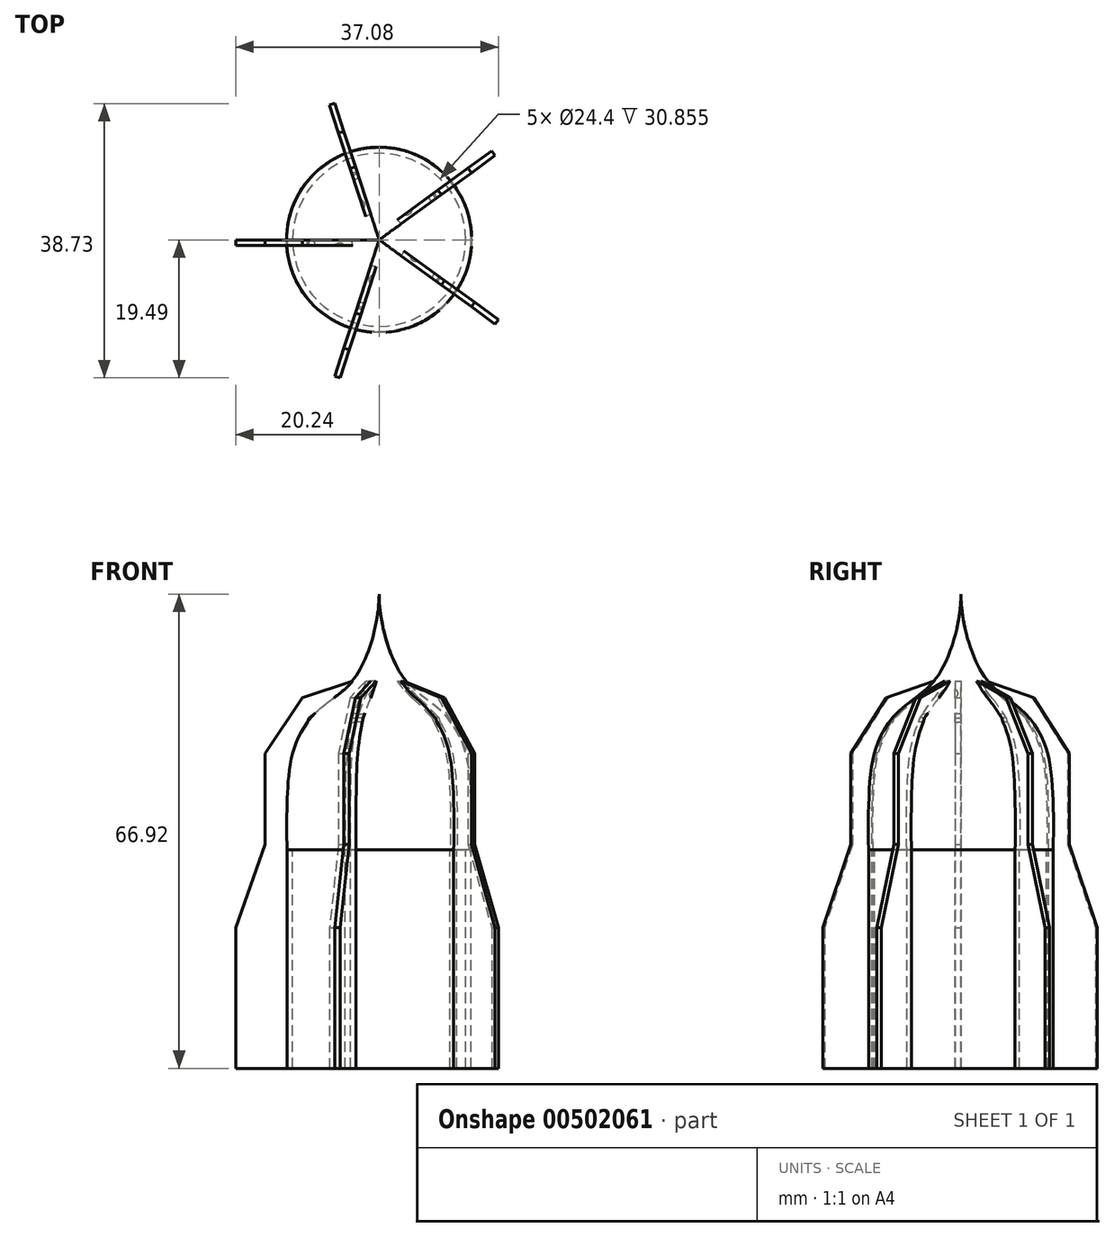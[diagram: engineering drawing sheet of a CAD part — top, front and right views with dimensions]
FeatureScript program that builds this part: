
annotation { "Feature Type Name" : "Feature", "Feature Type Description" : "" }
export const myFeature = defineFeature(function(context is Context, id is Id, definition is map)
    precondition{}
    {
        {
            var Q0;
            Q0=qCreatedBy(makeId("Front.planeOp"),FACE);
            var sketch = newSketch(context, id + "F0", { "sketchPlane" : qUnion([Q0])});
            skLineSegment(sketch, "E0", {"start": v(-12.2, 0) * mm, "end": v(-12.2, 30.85) * mm});
            skLineSegment(sketch, "E1", {"start": v(-13, 0) * mm, "end": v(-13, 30.85) * mm});
            skLineSegment(sketch, "E2", {"start": v(-12.2, 0) * mm, "end": v(-13, 0) * mm});
            skFitSpline(sketch, "E3", {"points": [v(-13, 30.85) * mm, v(-13, 37.68) * mm, v(-12.08, 45) * mm, v(-8.62, 50.53) * mm, v(-3.36, 55.23) * mm, v(0, 66.92) * mm], "startDerivative": vector(-1.92, 37.82) * mm, "endDerivative": vector(0, 44.37) * mm});
            skLineSegment(sketch, "E4", {"start": v(-12.2, 30.85) * mm, "end": v(0, 30.85) * mm});
            skLineSegment(sketch, "E5", {"start": v(0, 71.14) * mm, "end": v(0, -27.48) * mm});
            skSolve(sketch);
        }
        {
            var Q0;
            Q0=makeQuery(id+"F0.imprint","IMPRINT",FACE,{"disambiguationData":[TD([[makeQuery(id+"F0.imprint","IMPRINT",EDGE,{"derivedFrom":sQuery(id+"F0.wireOp",EDGE,"E0")}),1.0]])]});
            var Q1;
            Q1=sQuery(id+"F0.wireOp",EDGE,"E5");
            revolve(context, id + "F1", {"entities" : qUnion([Q0]), "axis" : qUnion([Q1]), "revolveType" : RevolveType.FULL});
        }
        {
            var Q0;
            Q0=qCreatedBy(makeId("Front.planeOp"),FACE);
            var sketch = newSketch(context, id + "F2", { "sketchPlane" : qUnion([Q0])});
            skLineSegment(sketch, "E6", {"start": v(-3.22, 54.82) * mm, "end": v(-10.83, 52.33) * mm});
            skLineSegment(sketch, "E7", {"start": v(-10.83, 52.33) * mm, "end": v(-16.09, 44.45) * mm});
            skLineSegment(sketch, "E8", {"start": v(-16.09, 44.45) * mm, "end": v(-16.09, 31.59) * mm});
            skLineSegment(sketch, "E9", {"start": v(-16.09, 31.59) * mm, "end": v(-20.24, 19.83) * mm});
            skLineSegment(sketch, "E10", {"start": v(-20.24, 19.83) * mm, "end": v(-20.24, 0) * mm});
            skLineSegment(sketch, "E11", {"start": v(-20.24, 0) * mm, "end": v(-12.63, 0) * mm});
            skLineSegment(sketch, "E12", {"start": v(-12.63, 0) * mm, "end": v(-12.63, 30.62) * mm});
            skLineSegment(sketch, "E13", {"start": v(-12.63, 30.62) * mm, "end": v(-12.63, 34.35) * mm});
            skLineSegment(sketch, "E14", {"start": v(-12.63, 34.35) * mm, "end": v(-12.63, 38.22) * mm});
            skLineSegment(sketch, "E15", {"start": v(-12.63, 38.22) * mm, "end": v(-12.63, 41.68) * mm});
            skLineSegment(sketch, "E16", {"start": v(-12.63, 41.68) * mm, "end": v(-11.66, 45.42) * mm});
            skLineSegment(sketch, "E17", {"start": v(-11.66, 45.42) * mm, "end": v(-9.86, 49.43) * mm});
            skLineSegment(sketch, "E18", {"start": v(-9.86, 49.43) * mm, "end": v(-3.22, 54.82) * mm});
            skSolve(sketch);
        }
        {
            var Q0;
            Q0=makeQuery(id+"F2.imprint","IMPRINT",FACE,{"disambiguationData":[TD([[makeQuery(id+"F2.imprint","IMPRINT",EDGE,{"derivedFrom":sQuery(id+"F2.wireOp",EDGE,"E6")}),1.0]])]});
            extrude(context, id + "F3", {"entities" : qUnion([Q0]), "operationType" : NewBodyOperationType.ADD, "depth" : 0.8 * mm});
        }
        {
            var Q0;
            Q0=makeQuery(id+"F1.opRevolve","SWEPT_BODY",BODY,{"disambiguationData":[OSD([sQuery(id+"F0.wireOp",EDGE,"E0"),sQuery(id+"F0.wireOp",EDGE,"E1"),sQuery(id+"F0.wireOp",EDGE,"E2"),sQuery(id+"F0.wireOp",EDGE,"E3"),sQuery(id+"F0.wireOp",EDGE,"E4"),sQuery(id+"F0.wireOp",EDGE,"E5")])]});
            var Q1;
            Q1=makeQuery(id+"F1.opRevolve","SWEPT_FACE",FACE,{"disambiguationData":[OSD([sQuery(id+"F0.wireOp",EDGE,"E1")])]});
            circularPattern(context, id + "F4", {"entities" : qUnion([Q0]), "axis" : qUnion([Q1]), "angle" : 360 * degree, "instanceCount" : 5, "equalSpace" : true});
        }
    });
